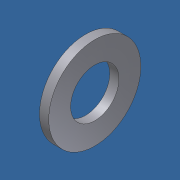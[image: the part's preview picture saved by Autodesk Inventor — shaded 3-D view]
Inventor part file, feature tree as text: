
AUTODESK INVENTOR PART (.ipt)
format: ipt  version: 2012 (Build 160160000, 160)  size: 96,256 bytes
history: native  units: mm (DEFAULTED — no unit token found)
features: other x1, plane x1
ambient origin geometry x7: Origin, YZ Plane, XY Plane, X Axis, Y Axis, Z Axis, Center Point
bodies: Solid1 (feature_tree), Body (feature_tree)
feature tree (2):
  other  "Work Axis1"
  plane  "Work Plane1"
